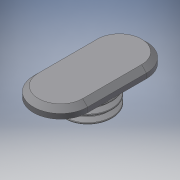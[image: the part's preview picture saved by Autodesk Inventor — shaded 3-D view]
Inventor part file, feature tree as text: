
AUTODESK INVENTOR PART (.ipt)
format: ipt  version: 2016 SP2 (Build 200236200, 236)  size: 414,208 bytes
history: native  units: mm
features: sketch x5, extrude x2, revolve x2, thread x1, other x1, chamfer x1
ambient origin geometry x8: Origin, YZ Plane, XZ Plane, XY Plane, X Axis, Y Axis, Z Axis, Center Point
bodies: Volumenkörper1 (feature_tree), Volumenkörper2 (feature_tree)
feature tree (12):
  extrude  "Extrusion1"  Depth=5.0mm TaperAngle=0.0deg
  thread  "Gewinde1"  [1 undecoded]
  revolve  "Umdrehung1"
  revolve  "Umdrehung2"
  other  "Spirale1"
  extrude  "Extrusion2"  Depth=1.5mm
  chamfer  "Fase1"  Distance=6.0mm
  sketch  "Skizze1"  dims[d0=9.5mm d1=5.0mm d2=0.0mm d3=10.0mm d4=0.0mm]
  sketch  "Skizze2"  dims[d5=60.0deg d6=0.240125mm d7=0.240125mm d10=1.5mm]
  sketch  "Skizze3"  dims[d12=60.0deg]
  sketch  "Skizze4"  dims[d14=0.0mm]
  sketch  "Skizze5"  dims[d15=0.0mm d16=1.5015mm d17=8.0mm d18=10.0mm d19=0.0mm d20=0.0mm d21=0.0mm d22=0.0mm d23=0.0mm d24=6.0mm d25=5.5mm d26=2.0mm d27=0.0mm d28=1.0mm d29=2.0mm d30=45.0deg]
note: 1 required parameter value undecoded (feature->parameter linkage not recoverable at this tier; creation-order binding heuristic only, values carry confidence <= 0.55)
